# Revit family: 84-05-003-DN80-100
name_source: partatom
category: Pipe Accessories
units: mm (PartAtom-declared; Revit-internal decimal feet)

## family parameters
Always vertical = Yes
Cut with Voids When Loaded = No
Part Type = Valve - Breaks Into
Round Connector Dimension = Use Diameter
Shared = No
Work Plane-Based = No

## types (6) — shared parameters
Bottom_Chamfer = 110 mm  [stored 0.360892 ft]
Bottom_Flange_Dia = 110 mm  [stored 0.360892 ft]
Bottom_Flange_Thickness = 20 mm  [stored 0.0656168 ft]
DN100-1000 = 84-100-05-211010
DN100-1250 = 84-100-05-311010
DN100-1500 = 84-100-05-411010
DN80-1000 = 84-080-05-211010
DN80-1250 = 84-080-05-311010
DN80-1500 = 84-080-05-411010
Description_ = AVK ABOVE-GROUND FIRE HYDRANT
Fillet = 40 mm  [stored 0.131234 ft]
Flange_width = 180 mm  [stored 0.590551 ft]
Flange_width_2 = 90 mm  [stored 0.295276 ft]
Flange_width_3 = 180 mm  [stored 0.590551 ft]
H6 = 875 mm  [stored 2.87073 ft]
L = 200 mm  [stored 0.656168 ft]
L2 = 126 mm  [stored 0.413386 ft]
Search_Table = 84-05-003-DN80-100
Top_Flange = 150 mm
Top_Flange_Thickness = 40 mm  [stored 0.131234 ft]
Top_Height_reference = 160 mm  [stored 0.524934 ft]
Top_Height_reference_2 = 300 mm
URL product pages = https://www.avkvalves.com

## per-type parameters (varying)
| type | DN | H3 | H8 | H9 | ID |
| 84-080-05-211010 | 80.1 mm  [stored 0.262795 ft] | 1865 mm  [stored 6.11877 ft] | 770 mm  [stored 2.52625 ft] | 220 mm  [stored 0.721785 ft] | 40.05 mm  [stored 0.131398 ft] |
| 84-080-05-311010 | 80.2 mm  [stored 0.263123 ft] | 2115 mm  [stored 6.93898 ft] | 1020 mm  [stored 3.34646 ft] | 220 mm  [stored 0.721785 ft] | 40.1 mm  [stored 0.131562 ft] |
| 84-080-05-411010 | 80.3 mm  [stored 0.263451 ft] | 2365 mm  [stored 7.75919 ft] | 1270 mm  [stored 4.16667 ft] | 220 mm  [stored 0.721785 ft] | 40.15 mm  [stored 0.131726 ft] |
| 84-100-05-211010 | 100.1 mm  [stored 0.328412 ft] | 1865 mm  [stored 6.11877 ft] | 725 mm  [stored 2.37861 ft] | 265 mm  [stored 0.869423 ft] | 50.05 mm  [stored 0.164206 ft] |
| 84-100-05-311010 | 100.2 mm  [stored 0.32874 ft] | 2115 mm  [stored 6.93898 ft] | 975 mm  [stored 3.19882 ft] | 265 mm  [stored 0.869423 ft] | 50.1 mm |
| 84-100-05-411010 | 100.3 mm  [stored 0.329068 ft] | 2365 mm  [stored 7.75919 ft] | 1225 mm  [stored 4.01903 ft] | 265 mm  [stored 0.869423 ft] | 50.15 mm |

note: [stored X ft] marks values corroborated as IEEE doubles in the binary element streams (Revit-internal decimal feet)

## geometry (parser evidence)
native form markers: Sweep x7
no freeform markers — native parametric forms only
